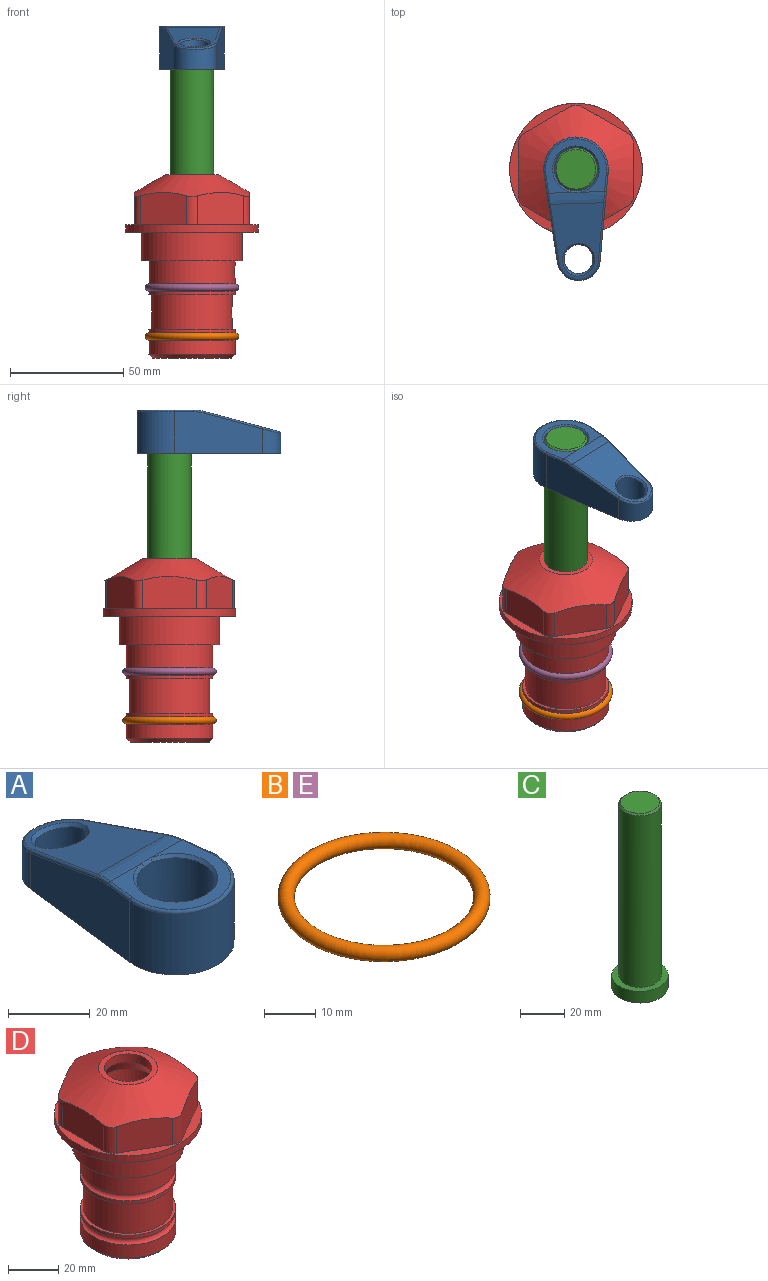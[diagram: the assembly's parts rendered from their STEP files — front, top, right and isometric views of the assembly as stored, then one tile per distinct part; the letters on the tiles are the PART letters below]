
ASSEMBLY  parts=5 mates=4
PART A: 31 faces, bbox 31.7x65.5x19.8 mm
  f0: plane 39.12x18.26mm, normal (0.99,0.12,0), area 612.2mm2, adj f1,f4,f7,f11,f13,f15
  f1: cylinder r=9.53mm len=18.91mm, axis (0,0,-1), area 296.1mm2, adj f0,f2,f7,f17
  f2: plane 39.12x18.26mm, normal (-0.99,0.12,0), area 612.2mm2, adj f1,f4,f7,f12,f14,f16
  f3: cylinder r=6.35mm len=12.7mm, axis (0,0,-1), area 362.4mm2, adj f7,f18
  f4: cylinder r=14.29mm len=28.58mm, axis (0,0,-1), area 882.2mm2, adj f0,f2,f7,f10
  f5: cylinder r=9.53mm len=19.05mm, axis (0,0,-1), area 1092.6mm2, adj f7,f19,f20
  f6: plane 26.99x23.69mm, normal (0,0,1), area 216.2mm2, adj f9,f10,f11,f12,f19
  f7: plane 63.5x28.58mm, normal (0,0,-1), area 661.8mm2, adj f0,f1,f2,f3,f4,f5,f22,f23
  f8: plane 33.52x23.6mm, normal (0,0.26,0.97), area 486mm2, adj f9,f15,f16,f17,f18
  f9: cylinder r=19.05mm len=24.72mm, axis (1,0,0), area 120.4mm2, adj f6,f8,f13,f14,f20
  f10: torus R=13.49mm, axis (0,0,1), area 59mm2, adj f4,f6,f11,f12
  f11: cylinder r=0.79mm len=8.67mm, axis (0.12,-0.99,0), area 10.8mm2, adj f0,f6,f10,f13
  f12: cylinder r=0.79mm len=8.67mm, axis (0.12,0.99,0), area 10.8mm2, adj f2,f6,f10,f14
  f13: bspline ~4.95x1.42mm, area 6.1mm2, adj f0,f9,f11,f15
  f14: bspline ~4.95x1.42mm, area 6.1mm2, adj f2,f9,f12,f16
  f15: cylinder r=0.79mm len=25.95mm, axis (0.12,-0.96,0.26), area 32.9mm2, adj f0,f8,f13,f17
  f16: cylinder r=0.79mm len=25.95mm, axis (0.12,0.96,-0.26), area 32.9mm2, adj f2,f8,f14,f17
  f17: bspline ~18.91x8.38mm, area 30mm2, adj f1,f8,f15,f16
  f18: bspline ~14.29x14.29mm, area 48.3mm2, adj f3,f8
  f19: cone r=9.53mm half-angle=45deg, axis (0,0,1), area 66.5mm2, adj f5,f6,f20
  f20: bspline ~3.22x0.96mm, area 3.5mm2, adj f5,f9,f19
  f21: plane 2.75x2.72mm, normal (0,0,-1), area 2.9mm2, adj f23,f25,f28
  f22: plane 23.05x15.88mm, normal (-0.99,-0.12,0), area 323.6mm2, adj f7,f25,f26,f27,f28,f29
  f23: plane 23.05x15.88mm, normal (0.99,-0.12,0), area 323.6mm2, adj f7,f21,f25,f27,f28,f30
  f24: cylinder r=9.53mm len=10.69mm, axis (0,0,-1), area 114.7mm2, adj f7,f27,f29,f30
  f25: cylinder r=12.7mm len=20.59mm, axis (0,0,-1), area 381.1mm2, adj f7,f21,f22,f23,f26,f28
  f26: plane 2.75x2.72mm, normal (0,0,-1), area 2.9mm2, adj f22,f25,f28
  f27: plane 19.72x18.37mm, normal (0,-0.26,-0.97), area 291.8mm2, adj f22,f23,f24,f28,f29,f30
  f28: cylinder r=15.88mm len=19.92mm, axis (1,0,0), area 54.8mm2, adj f21,f22,f23,f25,f26,f27
  f29: cylinder r=1.59mm len=11mm, axis (0,0,-1), area 34.7mm2, adj f7,f22,f24,f27
  f30: cylinder r=1.59mm len=11mm, axis (0,0,-1), area 34.7mm2, adj f7,f23,f24,f27
PART B: 1 faces, bbox 44.7x44.7x3.2 mm
  f0: torus R=19.05mm, axis (0,0,1), area 1193.9mm2
PART C: 6 faces, bbox 25.4x25.4x101.6 mm
  f0: plane 17.46x17.46mm, normal (0,0,1), area 239.5mm2, adj f5
  f1: plane 25.4x25.4mm, normal (0,0,-1), area 506.7mm2, adj f2
  f2: cylinder r=12.7mm len=25.4mm, axis (0,0,1), area 506.7mm2, adj f1,f3
  f3: plane 25.4x25.4mm, normal (0,0,1), area 221.7mm2, adj f2,f4
  f4: cylinder r=9.53mm len=94.46mm, axis (0,0,1), area 5653mm2, adj f3,f5
  f5: cone r=8.73mm half-angle=45deg, axis (0,0,-1), area 64.4mm2, adj f0,f4
PART D: 36 faces, bbox 58.7x58.7x81 mm
  f0: cylinder r=17.78mm len=35.56mm, axis (0,0,1), area 1670.8mm2, adj f23,f24,f31
  f1: cylinder r=19.05mm len=38.1mm, axis (0,0,1), area 1191.9mm2, adj f26,f27,f30
  f2: plane 58.66x58.66mm, normal (0,0,-1), area 1150.6mm2, adj f3,f28
  f3: cylinder r=29.33mm len=58.66mm, axis (0,0,-1), area 585.1mm2, adj f2,f4
  f4: plane 58.66x58.66mm, normal (0,0,1), area 475.9mm2, adj f3,f5,f6,f7,f8,f9,f10,f11
  f5: plane 20.32x14.34mm, normal (-0.5,0.87,0), area 324.4mm2, adj f4,f15,f16,f17
  f6: plane 20.32x14.34mm, normal (0.5,0.87,0), area 324.4mm2, adj f4,f14,f15,f17
  f7: plane 23.48x14.34mm, normal (1,0,0), area 324.4mm2, adj f4,f13,f14,f17
  f8: plane 20.32x14.34mm, normal (0.5,-0.87,0), area 324.4mm2, adj f4,f12,f13,f17
  f9: plane 20.32x14.34mm, normal (-0.5,-0.87,0), area 324.4mm2, adj f4,f11,f12,f17
  f10: plane 23.48x14.34mm, normal (-1,0,0), area 324.4mm2, adj f4,f11,f16,f17
  f11: cylinder r=5.08mm len=12.85mm, axis (0,0,-1), area 67.2mm2, adj f4,f9,f10,f17
  f12: cylinder r=5.08mm len=12.85mm, axis (0,0,-1), area 67.2mm2, adj f4,f8,f9,f17
  f13: cylinder r=5.08mm len=12.85mm, axis (0,0,-1), area 67.2mm2, adj f4,f7,f8,f17
  f14: cylinder r=5.08mm len=12.85mm, axis (0,0,-1), area 67.2mm2, adj f4,f6,f7,f17
  f15: cylinder r=5.08mm len=12.85mm, axis (0,0,-1), area 67.2mm2, adj f4,f5,f6,f17
  f16: cylinder r=5.08mm len=12.85mm, axis (0,0,-1), area 67.2mm2, adj f4,f5,f10,f17
  f17: cone r=11.73mm half-angle=60deg, axis (0,0,-1), area 2071.8mm2, adj f5,f6,f7,f8,f9,f10,f11,f12
  f18: plane 23.46x23.46mm, normal (0,0,1), area 147.4mm2, adj f17,f35
  f19: plane 34.93x34.93mm, normal (0,0,-1), area 958mm2, adj f29
  f20: cylinder r=19.05mm len=38.1mm, axis (0,0,1), area 760.1mm2, adj f21,f29
  f21: torus R=19.05mm, axis (0,0,1), area 565.3mm2, adj f20,f22
  f22: cylinder r=19.05mm len=38.1mm, axis (0,0,1), area 190mm2, adj f21,f23
  f23: plane 38.1x38.1mm, normal (0,0,1), area 146.9mm2, adj f0,f22
  f24: plane 38.1x38.1mm, normal (0,0,-1), area 146.9mm2, adj f0,f25
  f25: cylinder r=19.05mm len=38.1mm, axis (0,0,1), area 190mm2, adj f24,f26
  f26: torus R=19.05mm, axis (0,0,1), area 565.3mm2, adj f1,f25
  f27: plane 44.45x44.45mm, normal (0,0,-1), area 411.7mm2, adj f1,f28
  f28: cylinder r=22.23mm len=44.45mm, axis (0,0,1), area 1773.5mm2, adj f2,f27
  f29: cone r=19.05mm half-angle=45deg, axis (0,0,1), area 257.5mm2, adj f19,f20
  f30: cylinder r=3.17mm len=6.75mm, axis (-1,0,0), area 128mm2, adj f1,f33
  f31: cylinder r=3.17mm len=6.35mm, axis (-1,0,0), area 102.5mm2, adj f0,f33
  f32: plane 25.4x25.4mm, normal (0,0,1), area 506.7mm2, adj f33
  f33: cylinder r=12.7mm len=66.42mm, axis (0,0,-1), area 5236.2mm2, adj f30,f31,f32,f34
  f34: cone r=9.53mm half-angle=30deg, axis (0,0,-1), area 443.4mm2, adj f33,f35
  f35: cylinder r=9.53mm len=19.05mm, axis (0,0,-1), area 240.9mm2, adj f18,f34
PART E: same geometry as B
PLACE A rot(axis=(0,0,-1),178.3deg) t=(0,0,27.55)mm
PLACE B t=(0,0,-21.59)mm
PLACE C rot(axis=(0,0,-1),178.3deg) t=(0,0,27.55)mm
PLACE D at identity fixed
PLACE E at identity
MATE fastened B.f0 <-> D.f0  axis (0,0,1) through (0,0,-46.1)mm
MATE cylindrical D.f0 <-> C.f2  axis (0,0,1) through (0,0,-50.55)mm
MATE fastened C.f2 <-> A.f4  axis (0,0,1) through (0,0,91.05)mm
MATE fastened E.f0 <-> D.f0  axis (0,0,1) through (0,0,-24.51)mm
